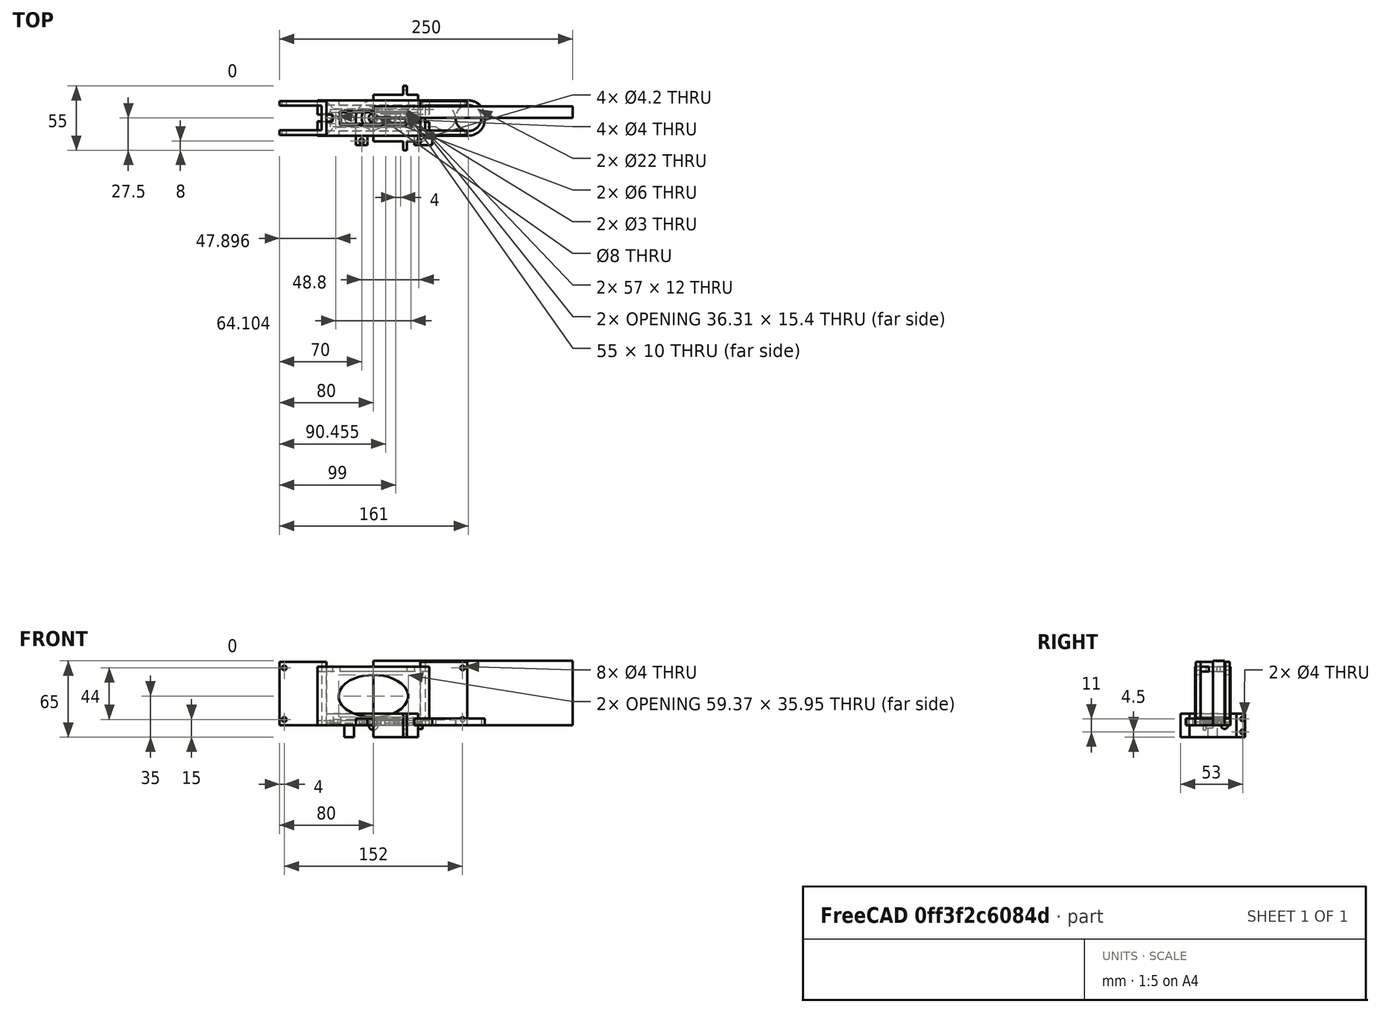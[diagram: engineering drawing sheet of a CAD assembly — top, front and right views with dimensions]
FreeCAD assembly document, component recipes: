
FREECAD ASSEMBLY — COMPONENT RECIPES ("assembly_05")

This assembly document has 12 components, labeled P0..P11 below (a component is one placed body or linked part). 12 of them carry a construction recipe — the FreeCAD feature program that regenerates the part from scratch, quoted from this document or its linked companion documents; the rest are supplied as boundary geometry only. No exploded tour is included for this assembly.
COMPONENT P0 — recipe-attached ("lower_leg", modeled in this document).
Construction recipe (the document's own serialized feature program — sketch geometry with constraints, then the solid features built on it; lengths are millimeters unless a unit is written):

FEATURE [Sketcher::SketchObject] Sketch
  FullyConstrained = true
  MapMode = 5
  Support = -> [XY_Plane001]
  sketch-geometry (4):
    g0: LineSegment StartX=53.3856 StartY=-7.50386 StartZ=0 EndX=-36.6144 EndY=-7.50386 EndZ=0
    g1: LineSegment StartX=-36.6144 StartY=-7.50386 StartZ=0 EndX=-36.6144 EndY=7.49614 EndZ=0
    g2: LineSegment StartX=-36.6144 StartY=7.49614 StartZ=0 EndX=53.3856 EndY=7.50386 EndZ=0
    g3: ArcOfCircle CenterX=59.9956 CenterY=0 CenterZ=0 NormalX=0 NormalY=0 NormalZ=1 AngleXU=0 Radius=10 StartAngle=3.99024 EndAngle=8.57613
  constraints (13):
    c: Coincident(g0,g1)
    c: Coincident(g1,g2)
    c: Horizontal(g0)
    c: Vertical(g1)
    c: Diameter(g3) = 20
    c: PointOnObject(g3,g-1)
    c: Coincident(g2,g3)
    c: Coincident(g0,g3)
    c: DistanceX(g0,g0) = 90
    c: DistanceY(g1,g1) = 15
    c: DistanceX(g2,g3) = 6.61
    c: DistanceX(g2) = 53.3856
    c: DistanceX(g2,g2) = 90
FEATURE [PartDesign::Pad] Pad
  Direction = (0,0,1)
  Length = 5
  Length2 = 10
  Profile = -> Sketch
  ReferenceAxis = -> Sketch [N_Axis]
  Type = 0
FEATURE [Sketcher::SketchObject] Sketch047
  ExternalGeometry = -> [Pad]
  FullyConstrained = true
  MapMode = 5
  Placement = pos=(0,0,0) rot=(1,0,0;3.14159rad)
  Support = -> [Pad]
  sketch-geometry (1):
    g0: Circle CenterX=-20.6144 CenterY=0 CenterZ=0 NormalX=0 NormalY=0 NormalZ=1 AngleXU=0 Radius=4.1
  constraints (3):
    c: PointOnObject(g0,g-1)
    c: DistanceX(g-3,g0) = 16
    c: Diameter(g0) = 8.2
FEATURE [PartDesign::Pad] Pad029
  BaseFeature = -> Pad
  Direction = (0,0,-1)
  Length = 10
  Length2 = 10
  Profile = -> Sketch047
  ReferenceAxis = -> Sketch047 [N_Axis]
  Type = 0
FEATURE [Sketcher::SketchObject] Sketch052
  ExternalGeometry = -> [Sketch,Pad029]
  FullyConstrained = true
  MapMode = 5
  Placement = pos=(0,0,0) rot=(1,0,0;3.14159rad)
  Support = -> [Pad029]
  sketch-geometry (1):
    g0: Circle CenterX=-32.1044 CenterY=0 CenterZ=0 NormalX=0 NormalY=0 NormalZ=1 AngleXU=0 Radius=2
  constraints (3):
    c: PointOnObject(g0,g-1)
    c: Diameter(g0) = 4
    c: Distance(g0,g-3) = 4.51
FEATURE [PartDesign::Pocket] Pocket
  BaseFeature = -> Pad029
  Direction = (0,0,1)
  Length = 5
  Length2 = 5
  Profile = -> Sketch052
  ReferenceAxis = -> Sketch052 [N_Axis]
  Type = 0
FEATURE [PartDesign::CoordinateSystem] Local_CS014
  AttacherType = Attacher::AttachEngine3D
  MapMode = 45
  Placement = pos=(-32.1044,0,2.5) rot=(0,0,1;0rad)
  Support = -> [Pocket]
FEATURE [PartDesign::CoordinateSystem] Local_CS015
  AttacherType = Attacher::AttachEngine3D
  MapMode = 45
  Placement = pos=(-20.6144,1e-16,-10) rot=(0,0,1;0rad)
  Support = -> [Pocket]
FEATURE [PartDesign::CoordinateSystem] Local_CS039
  AttacherType = Attacher::AttachEngine3D
  MapMode = 11
  Placement = pos=(-20.6144,0,0) rot=(0.707107,-0.707107,0;3.14159rad)
  Support = -> [Sketch047]
FEATURE [PartDesign::Body] Body  label="lower_leg"
  Group = -> [Sketch,Pad,Sketch047,Pad029,Sketch052,Pocket,Local_CS014,Local_CS015,Local_CS039]
  Origin = -> Origin001
  Tip = -> Pocket
COMPONENT P1 — recipe-attached ("leg_connector", modeled in this document).
Construction recipe (the document's own serialized feature program — sketch geometry with constraints, then the solid features built on it; lengths are millimeters unless a unit is written):

FEATURE [Sketcher::SketchObject] Sketch049
  FullyConstrained = true
  MapMode = 5
  Support = -> [XY_Plane014]
  sketch-geometry (4):
    g0: LineSegment StartX=-40 StartY=5 StartZ=0 EndX=40 EndY=5 EndZ=0
    g1: LineSegment StartX=40 StartY=5 StartZ=0 EndX=40 EndY=-5 EndZ=0
    g2: LineSegment StartX=40 StartY=-5 StartZ=0 EndX=-40 EndY=-5 EndZ=0
    g3: LineSegment StartX=-40 StartY=-5 StartZ=0 EndX=-40 EndY=5 EndZ=0
  constraints (10):
    c: Coincident(g0,g1)
    c: Coincident(g1,g2)
    c: Coincident(g2,g3)
    c: Coincident(g3,g0)
    c: Horizontal(g2)
    c: Vertical(g3)
    c: Symmetric(g0,g1,g-1)
    c: Symmetric(g0,g0,g-2)
    c: DistanceX(g0,g0) = 80
    c: DistanceY(g1,g1) = 10
FEATURE [PartDesign::Pad] Pad030
  Direction = (0,0,1)
  Length = 2
  Length2 = 10
  Profile = -> Sketch049
  ReferenceAxis = -> Sketch049 [N_Axis]
  Type = 0
FEATURE [Sketcher::SketchObject] Sketch050
  ExternalGeometry = -> [Pad030]
  FullyConstrained = true
  MapMode = 5
  Placement = pos=(0,0,2) rot=(0,0,1;0rad)
  Support = -> [Pad030]
  sketch-geometry (2):
    g0: Circle CenterX=-32 CenterY=0 CenterZ=0 NormalX=0 NormalY=0 NormalZ=1 AngleXU=0 Radius=2
    g1: Circle CenterX=32 CenterY=0 CenterZ=0 NormalX=0 NormalY=0 NormalZ=1 AngleXU=0 Radius=2
  constraints (5):
    c: PointOnObject(g0,g-1)
    c: Diameter(g1) = 4
    c: Diameter(g0) = 4
    c: Symmetric(g1,g0,g-2)
    c: DistanceX(g0,g1) = 64
FEATURE [PartDesign::Pocket] Pocket023
  BaseFeature = -> Pad030
  Direction = (0,0,-1)
  Length = 5
  Length2 = 5
  Profile = -> Sketch050
  ReferenceAxis = -> Sketch050 [N_Axis]
  Type = 0
FEATURE [PartDesign::Fillet] Fillet
  Base = -> Pocket023 [Edge8,Edge2,Edge5,Edge1]
  BaseFeature = -> Pocket023
  Radius = 4
  SupportTransform = false
  UseAllEdges = false
FEATURE [PartDesign::CoordinateSystem] Local_CS
  AttacherType = Attacher::AttachEngine3D
  MapMode = 45
  Placement = pos=(32,0,1) rot=(0,0,1;0rad)
  Support = -> [Fillet]
FEATURE [PartDesign::CoordinateSystem] Local_CS019
  AttacherType = Attacher::AttachEngine3D
  MapMode = 45
  Placement = pos=(-32,0,1) rot=(0,0,1;0rad)
  Support = -> [Fillet]
FEATURE [PartDesign::Body] Body012  label="leg_connector"
  Group = -> [Sketch049,Pad030,Sketch050,Pocket023,Fillet,Local_CS,Local_CS019]
  Origin = -> Origin014
  Tip = -> Fillet
COMPONENT P2 — recipe-attached ("servo", modeled in this document).
Construction recipe (the document's own serialized feature program — sketch geometry with constraints, then the solid features built on it; lengths are millimeters unless a unit is written):

FEATURE [PartDesign::Plane] DatumPlane
  AttachmentOffset = pos=(0,0,25.5) rot=(0,0,1;0rad)
  Length = 65.4881
  MapMode = 5
  Placement = pos=(25.5,-5.7e-15,5.7e-15) rot=(0.57735,0.57735,0.57735;2.0944rad)
  ResizeMode = 0
  Support = -> [YZ_Plane015]
  Width = 60.4881
FEATURE [Sketcher::SketchObject] Sketch055
  FullyConstrained = true
  MapMode = 5
  Placement = pos=(25.5,-5.7e-15,5.7e-15) rot=(0.57735,0.57735,0.57735;2.0944rad)
  Support = -> [DatumPlane]
  sketch-geometry (8):
    g0: LineSegment StartX=-27.5 StartY=10 StartZ=0 EndX=27.5 EndY=10 EndZ=0
    g1: LineSegment StartX=27.5 StartY=10 StartZ=0 EndX=27.5 EndY=-10 EndZ=0
    g2: LineSegment StartX=27.5 StartY=-10 StartZ=0 EndX=-27.5 EndY=-10 EndZ=0
    g3: LineSegment StartX=-27.5 StartY=-10 StartZ=0 EndX=-27.5 EndY=10 EndZ=0
    g4: Circle CenterX=-25.5 CenterY=5.5 CenterZ=0 NormalX=0 NormalY=0 NormalZ=1 AngleXU=0 Radius=2
    g5: Circle CenterX=-25.5 CenterY=-5.5 CenterZ=0 NormalX=0 NormalY=0 NormalZ=1 AngleXU=0 Radius=2
    g6: Circle CenterX=25.5 CenterY=5.5 CenterZ=0 NormalX=0 NormalY=0 NormalZ=1 AngleXU=0 Radius=2
    g7: Circle CenterX=25.5 CenterY=-5.5 CenterZ=0 NormalX=0 NormalY=0 NormalZ=1 AngleXU=0 Radius=2
  constraints (22):
    c: Coincident(g0,g1)
    c: Coincident(g1,g2)
    c: Coincident(g2,g3)
    c: Coincident(g3,g0)
    c: Horizontal(g2)
    c: Vertical(g3)
    c: Symmetric(g0,g0,g-2)
    c: Symmetric(g0,g1,g-1)
    c: DistanceY(g1,g1) = 20
    c: DistanceX(g0,g0) = 55
    c: Diameter(g4) = 4
    c: Diameter(g5) = 4
    c: Diameter(g6) = 4
    c: Diameter(g7) = 4
    c: DistanceY(g4,g0) = 4.5
    c: DistanceY(g6,g0) = 4.5
    c: DistanceY(g2,g5) = 4.5
    c: DistanceY(g1,g7) = 4.5
    c: DistanceX(g0,g4) = 2
    c: DistanceX(g2,g5) = 2
    c: DistanceX(g6,g0) = 2
    c: DistanceX(g7,g1) = 2
FEATURE [Sketcher::SketchObject] Sketch054
  FullyConstrained = true
  MapMode = 5
  Placement = pos=(0,0,0) rot=(0.57735,0.57735,0.57735;2.0944rad)
  Support = -> [YZ_Plane015]
  sketch-geometry (4):
    g0: LineSegment StartX=-20 StartY=10 StartZ=0 EndX=20 EndY=10 EndZ=0
    g1: LineSegment StartX=20 StartY=10 StartZ=0 EndX=20 EndY=-10 EndZ=0
    g2: LineSegment StartX=20 StartY=-10 StartZ=0 EndX=-20 EndY=-10 EndZ=0
    g3: LineSegment StartX=-20 StartY=-10 StartZ=0 EndX=-20 EndY=10 EndZ=0
  constraints (10):
    c: Coincident(g0,g1)
    c: Coincident(g1,g2)
    c: Coincident(g2,g3)
    c: Coincident(g3,g0)
    c: Horizontal(g2)
    c: Vertical(g3)
    c: Symmetric(g0,g0,g-2)
    c: Symmetric(g0,g1,g-1)
    c: DistanceX(g0,g0) = 40
    c: DistanceY(g1,g1) = 20
FEATURE [PartDesign::Pad] Pad034
  Direction = (1,-2e-16,3e-16)
  Length = 38
  Length2 = 10
  Placement = pos=(0,0,0) rot=(0.57735,0.57735,0.57735;2.0944rad)
  Profile = -> Sketch054
  ReferenceAxis = -> Sketch054 [N_Axis]
  Type = 0
FEATURE [PartDesign::Pad] Pad035
  BaseFeature = -> Pad034
  Direction = (1,-1e-16,1e-16)
  Length = 3
  Length2 = 10
  Placement = pos=(0,0,0) rot=(0.57735,0.57735,0.57735;2.0944rad)
  Profile = -> Sketch055
  ReferenceAxis = -> Sketch055 [N_Axis]
  Type = 0
FEATURE [Sketcher::SketchObject] Sketch056
  ExternalGeometry = -> [Pad035]
  FullyConstrained = true
  MapMode = 5
  Placement = pos=(38,-8.4e-15,8.4e-15) rot=(0.57735,0.57735,0.57735;2.0944rad)
  Support = -> [Pad035]
  sketch-geometry (1):
    g0: Circle CenterX=10 CenterY=0 CenterZ=0 NormalX=0 NormalY=0 NormalZ=1 AngleXU=0 Radius=3
  constraints (3):
    c: PointOnObject(g0,g-1)
    c: Diameter(g0) = 6
    c: DistanceX(g0,g-3) = 10
FEATURE [PartDesign::Pad] Pad036
  BaseFeature = -> Pad035
  Direction = (1,-9e-16,6e-16)
  Length = 4
  Length2 = 10
  Placement = pos=(0,0,0) rot=(0.57735,0.57735,0.57735;2.0944rad)
  Profile = -> Sketch056
  ReferenceAxis = -> Sketch056 [N_Axis]
  Type = 0
FEATURE [PartDesign::CoordinateSystem] Local_CS009
  AttacherType = Attacher::AttachEngine3D
  MapMode = 45
  Placement = pos=(27,25.5,-5.5) rot=(0.57735,0.57735,0.57735;2.0944rad)
  Support = -> [Pad036]
FEATURE [PartDesign::CoordinateSystem] Local_CS010
  AttacherType = Attacher::AttachEngine3D
  MapMode = 45
  Placement = pos=(27,25.5,5.5) rot=(0.57735,0.57735,0.57735;2.0944rad)
  Support = -> [Pad036]
FEATURE [PartDesign::CoordinateSystem] Local_CS011  label="lcs_lever_adapter"
  AttacherType = Attacher::AttachEngine3D
  MapMode = 45
  Placement = pos=(42,10,1.82e-14) rot=(0.57735,0.57735,0.57735;2.0944rad)
  Support = -> [Pad036]
FEATURE [PartDesign::CoordinateSystem] Local_CS020
  AttacherType = Attacher::AttachEngine3D
  MapMode = 45
  Placement = pos=(0,-1e-16,7e-16) rot=(0.707107,0,0.707107;3.14159rad)
  Support = -> [Pad036]
FEATURE [PartDesign::CoordinateSystem] Local_CS043  label="servo_bottom_lcs"
  AttacherType = Attacher::AttachEngine3D
  MapMode = 5
  Placement = pos=(0,0,0) rot=(0.57735,0.57735,-0.57735;4.18879rad)
  Support = -> [Pad036]
FEATURE [PartDesign::Body] Body013  label="servo"
  Group = -> [Sketch054,Pad034,DatumPlane,Sketch055,Pad035,Sketch056,Pad036,Local_CS009,Local_CS010,Local_CS011,Local_CS020,Local_CS043]
  Origin = -> Origin015
  Tip = -> Pad036
COMPONENT P3 — recipe-attached ("connector_bolt", modeled in this document).
Construction recipe (the document's own serialized feature program — sketch geometry with constraints, then the solid features built on it; lengths are millimeters unless a unit is written):

FEATURE [Sketcher::SketchObject] Sketch077
  FullyConstrained = true
  MapMode = 5
  Placement = pos=(0,0,0) rot=(1,0,0;1.5708rad)
  Support = -> [XZ_Plane018]
  sketch-geometry (1):
    g0: Circle CenterX=0 CenterY=0 CenterZ=0 NormalX=0 NormalY=0 NormalZ=1 AngleXU=0 Radius=2
  constraints (2):
    c: Coincident(g0,g-1)
    c: Diameter(g0) = 4
FEATURE [PartDesign::Pad] Pad048
  Direction = (0,-1,2e-16)
  Length = 6
  Length2 = 10
  Placement = pos=(0,0,0) rot=(1,0,0;1.5708rad)
  Profile = -> Sketch077
  ReferenceAxis = -> Sketch077 [N_Axis]
  Type = 0
FEATURE [Sketcher::SketchObject] Sketch078
  FullyConstrained = true
  MapMode = 5
  Placement = pos=(0,-6,1.3e-15) rot=(1,0,0;1.5708rad)
  Support = -> [Pad048]
  sketch-geometry (1):
    g0: Circle CenterX=0 CenterY=0 CenterZ=0 NormalX=0 NormalY=0 NormalZ=1 AngleXU=0 Radius=4
  constraints (2):
    c: Coincident(g0,g-1)
    c: Diameter(g0) = 8
FEATURE [PartDesign::Pad] Pad049
  BaseFeature = -> Pad048
  Direction = (0,-1,2e-16)
  Length = 2
  Length2 = 10
  Placement = pos=(0,0,0) rot=(1,0,0;1.5708rad)
  Profile = -> Sketch078
  ReferenceAxis = -> Sketch078 [N_Axis]
  Type = 0
FEATURE [PartDesign::CoordinateSystem] Local_CS025
  AttacherType = Attacher::AttachEngine3D
  MapMode = 45
  Placement = pos=(0,-3,1.2e-15) rot=(0,0.707107,0.707107;3.14159rad)
  Support = -> [Pad049]
FEATURE [PartDesign::Body] Body016  label="connector_bolt"
  Group = -> [Sketch077,Pad048,Sketch078,Pad049,Local_CS025]
  Origin = -> Origin018
  Tip = -> Pad049
COMPONENT P4 — recipe-attached ("upper_leg_left", modeled in this document).
Construction recipe (the document's own serialized feature program — sketch geometry with constraints, then the solid features built on it; lengths are millimeters unless a unit is written):

FEATURE [Sketcher::SketchObject] Sketch084
  FullyConstrained = false
  MapMode = 5
  Placement = pos=(0,0,0) rot=(1,0,0;3.14159rad)
  sketch-geometry (4):
    g0: LineSegment StartX=13.6097 StartY=7.7 StartZ=0 EndX=28.6097 EndY=7.7 EndZ=0
    g1: LineSegment StartX=28.6097 StartY=7.7 StartZ=0 EndX=28.6097 EndY=-7.7 EndZ=0
    g2: LineSegment StartX=28.6097 StartY=-7.7 StartZ=0 EndX=13.6097 EndY=-7.7 EndZ=0
    g3: LineSegment StartX=13.6097 StartY=-7.7 StartZ=0 EndX=13.6097 EndY=7.7 EndZ=0
  constraints (8):
    c: Coincident(g0,g1)
    c: Coincident(g1,g2)
    c: Coincident(g2,g3)
    c: Coincident(g3,g0)
    c: Horizontal(g0)
    c: Horizontal(g2)
    c: Vertical(g1)
    c: Vertical(g3)
FEATURE [Sketcher::SketchObject] Sketch079
  FullyConstrained = false
  MapMode = 5
  Support = -> [XY_Plane019]
  sketch-geometry (12):
    g0: ArcOfCircle CenterX=0 CenterY=0 CenterZ=0 NormalX=0 NormalY=0 NormalZ=1 AngleXU=0 Radius=7.7 StartAngle=1.5708 EndAngle=4.71239
    g1: LineSegment StartX=28.6097 StartY=-3.8 StartZ=0 EndX=13.6097 EndY=-3.8 EndZ=0
    g2: LineSegment StartX=13.6097 StartY=3.8 StartZ=0 EndX=28.6097 EndY=3.8 EndZ=0
    g3: LineSegment StartX=28.6097 StartY=3.8 StartZ=0 EndX=28.6097 EndY=-3.8 EndZ=0
    g4: LineSegment StartX=-1.2e-15 StartY=7.7 StartZ=0 EndX=13.6097 EndY=7.7 EndZ=0
    g5: LineSegment StartX=13.6097 StartY=7.7 StartZ=0 EndX=13.6097 EndY=3.8 EndZ=0
    g6: LineSegment StartX=-1.4e-15 StartY=-7.7 StartZ=0 EndX=13.6097 EndY=-7.7 EndZ=0
    g7: LineSegment StartX=13.6097 StartY=-7.7 StartZ=0 EndX=13.6097 EndY=-3.8 EndZ=0
    g8: LineSegment StartX=-15 StartY=15 StartZ=0 EndX=95 EndY=15 EndZ=0
    g9: LineSegment StartX=95 StartY=15 StartZ=0 EndX=95 EndY=-15 EndZ=0
    g10: LineSegment StartX=95 StartY=-15 StartZ=0 EndX=-15 EndY=-15 EndZ=0
    g11: LineSegment StartX=-15 StartY=-15 StartZ=0 EndX=-15 EndY=15 EndZ=0
  constraints (31):
    c: Coincident(g0,g-1)
    c: Diameter(g0) = 15.4
    c: Coincident(g2,g3)
    c: Coincident(g3,g1)
    c: Horizontal(g1)
    c: Horizontal(g2)
    c: Symmetric(g1,g2,g-1)
    c: DistanceY(g3,g3) = 7.6
    c: Horizontal(g4)
    c: Coincident(g4,g5)
    c: Vertical(g5)
    c: DistanceX(g5,g2) = 15
    c: Horizontal(g6)
    c: Coincident(g6,g7)
    c: Vertical(g7)
    c: DistanceX(g7,g1) = 15
    c: Tangent(g0,g4) = 1.5708
    c: Coincident(g2,g5)
    c: Coincident(g1,g7)
    c: Tangent(g0,g6) = -1.5708
    c: Coincident(g8,g9)
    c: Coincident(g9,g10)
    c: Coincident(g10,g11)
    c: Coincident(g11,g8)
    c: Horizontal(g8)
    c: Horizontal(g10)
    c: Vertical(g9)
    c: Symmetric(g8,g10,g-1)
    c: DistanceY(g11,g11) = 30
    c: DistanceX(g10,g-1) = 15
    c: DistanceX(g-1,g9) = 95
FEATURE [PartDesign::Pad] Pad050
  Direction = (0,0,1)
  Length = 6
  Length2 = 10
  Profile = -> Sketch079
  ReferenceAxis = -> Sketch079 [N_Axis]
  Type = 0
FEATURE [Sketcher::SketchObject] Sketch080
  ExternalGeometry = -> [Pad050]
  FullyConstrained = true
  MapMode = 5
  Placement = pos=(0,-15,0) rot=(1,0,0;1.5708rad)
  Support = -> [Pad050]
  sketch-geometry (4):
    g0: LineSegment StartX=-15 StartY=6 StartZ=0 EndX=50 EndY=6 EndZ=0
    g1: LineSegment StartX=50 StartY=6 StartZ=0 EndX=50 EndY=0 EndZ=0
    g2: LineSegment StartX=50 StartY=0 StartZ=0 EndX=-15 EndY=0 EndZ=0
    g3: LineSegment StartX=-15 StartY=0 StartZ=0 EndX=-15 EndY=6 EndZ=0
  constraints (11):
    c: Coincident(g0,g1)
    c: Coincident(g1,g2)
    c: Coincident(g2,g3)
    c: Coincident(g3,g0)
    c: Horizontal(g0)
    c: Horizontal(g2)
    c: Vertical(g1)
    c: Vertical(g3)
    c: Coincident(g0,g-4)
    c: PointOnObject(g1,g-5)
    c: DistanceX(g0,g0) = 65
FEATURE [Sketcher::SketchObject] Sketch081
  FullyConstrained = false
  MapMode = 5
  Placement = pos=(0,0,-3e-15) rot=(1,0,0;3.14159rad)
  sketch-geometry (2):
    g0: Circle CenterX=-10 CenterY=19.5 CenterZ=0 NormalX=0 NormalY=0 NormalZ=1 AngleXU=0 Radius=2.1
    g1: Circle CenterX=38.8 CenterY=19.5 CenterZ=0 NormalX=0 NormalY=0 NormalZ=1 AngleXU=0 Radius=2.1
  constraints (5):
    c: DistanceY(g0,g1) = 0
    c: DistanceX(g0,g1) = 48.8
    c: Diameter(g1) = 4.2
    c: Diameter(g0) = 4.2
    c: DistanceY(g-1,g0) = 19.5
FEATURE [PartDesign::Pad] Pad051
  BaseFeature = -> Pad050
  Direction = (0,-1,2e-16)
  Length = 8
  Length2 = 10
  Profile = -> Sketch080
  ReferenceAxis = -> Sketch080 [N_Axis]
  Type = 0
FEATURE [PartDesign::Pocket] Pocket024
  BaseFeature = -> Pad051
  Direction = (0,0,1)
  Length = 5
  Length2 = 5
  Midplane = true
  Profile = -> Sketch081
  ReferenceAxis = -> Sketch081 [N_Axis]
  Type = 1
FEATURE [Sketcher::SketchObject] Sketch082
  ExternalGeometry = -> [Sketch080,Pocket024]
  FullyConstrained = false
  MapMode = 5
  Placement = pos=(0,1.3e-15,6) rot=(0,0,1;0rad)
  Support = -> [Pocket024]
  sketch-geometry (4):
    g0: LineSegment StartX=-5 StartY=-34 StartZ=0 EndX=35 EndY=-34 EndZ=0
    g1: LineSegment StartX=35 StartY=-34 StartZ=0 EndX=35 EndY=-15 EndZ=0
    g2: LineSegment StartX=35 StartY=-15 StartZ=0 EndX=-5 EndY=-15 EndZ=0
    g3: LineSegment StartX=-5 StartY=-15 StartZ=0 EndX=-5 EndY=-34 EndZ=0
  constraints (11):
    c: Coincident(g0,g1)
    c: Coincident(g1,g2)
    c: Coincident(g2,g3)
    c: Coincident(g3,g0)
    c: Horizontal(g0)
    c: Horizontal(g2)
    c: Vertical(g1)
    c: Vertical(g3)
    c: DistanceX(g-5,g2) = 10
    c: PointOnObject(g2,g-3)
    c: DistanceX(g0,g0) = 40
FEATURE [PartDesign::Pocket] Pocket025
  BaseFeature = -> Pocket024
  Direction = (0,-2e-16,-1)
  Length = 3
  Length2 = 5
  Midplane = true
  Profile = -> Sketch082
  ReferenceAxis = -> Sketch082 [N_Axis]
  Type = 1
FEATURE [Sketcher::SketchObject] Sketch083
  ExternalGeometry = -> [Pocket025]
  FullyConstrained = true
  MapMode = 5
  Placement = pos=(0,0,6) rot=(0,0,1;0rad)
  Support = -> [Pocket025]
  sketch-geometry (1):
    g0: Circle CenterX=81 CenterY=0 CenterZ=0 NormalX=0 NormalY=0 NormalZ=1 AngleXU=0 Radius=11
  constraints (3):
    c: PointOnObject(g0,g-1)
    c: Diameter(g0) = 22
    c: DistanceX(g0,g-3) = 14
FEATURE [PartDesign::Pocket] Pocket026
  BaseFeature = -> Pocket025
  Direction = (0,0,-1)
  Length = 5
  Length2 = 5
  Midplane = true
  Profile = -> Sketch083
  ReferenceAxis = -> Sketch083 [N_Axis]
  Type = 1
FEATURE [PartDesign::Fillet] Fillet014
  Base = -> Pocket026 [Edge8,Edge2]
  BaseFeature = -> Pocket026
  Radius = 14
  SupportTransform = false
  UseAllEdges = false
FEATURE [PartDesign::Fillet] Fillet015
  Base = -> Fillet014 [Edge3]
  BaseFeature = -> Fillet014
  Radius = 15
  SupportTransform = false
  UseAllEdges = false
FEATURE [PartDesign::Fillet] Fillet016
  Base = -> Fillet015
  BaseFeature = -> Fillet015
  Radius = 3
  SupportTransform = false
  UseAllEdges = false
FEATURE [PartDesign::Pad] Pad052
  BaseFeature = -> Fillet016
  Direction = (0,0,-1)
  Length = 2
  Length2 = 10
  Profile = -> Sketch084
  ReferenceAxis = -> Sketch084 [N_Axis]
  Reversed = true
  Type = 0
FEATURE [PartDesign::CoordinateSystem] Local_CS026
  AttacherType = Attacher::AttachEngine3D
  MapMode = 45
  Placement = pos=(38.8,-19.5,3) rot=(0,0,1;0rad)
  Support = -> [Pad052]
FEATURE [PartDesign::CoordinateSystem] Local_CS027
  AttacherType = Attacher::AttachEngine3D
  MapMode = 45
  Placement = pos=(-10,-19.5,3) rot=(0,0,1;0rad)
  Support = -> [Pad052]
FEATURE [PartDesign::CoordinateSystem] Local_CS028
  AttacherType = Attacher::AttachEngine3D
  MapMode = 45
  Placement = pos=(81,-8e-16,3) rot=(0,0,1;0rad)
  Support = -> [Pad052]
FEATURE [PartDesign::CoordinateSystem] Local_CS029
  AttacherType = Attacher::AttachEngine3D
  MapMode = 45
  Placement = pos=(1.29631,4e-16,3) rot=(0,0,1;0rad)
  Support = -> [Pad052]
FEATURE [PartDesign::Body] Body017  label="upper_leg_left"
  Group = -> [Sketch079,Pad050,Sketch080,Pad051,Sketch081,Pocket024,Sketch082,Pocket025,Sketch083,Pocket026,Fillet014,Fillet015,Fillet016,Sketch084,Pad052,Local_CS026,Local_CS027,Local_CS028,Local_CS029]
  Origin = -> Origin019
  Tip = -> Pad052
COMPONENT P5 — recipe-attached ("upper_leg_right", modeled in this document).
Construction recipe (the document's own serialized feature program — sketch geometry with constraints, then the solid features built on it; lengths are millimeters unless a unit is written):

FEATURE [Sketcher::SketchObject] Sketch085
  FullyConstrained = false
  MapMode = 5
  Support = -> [XY_Plane020]
  sketch-geometry (12):
    g0: ArcOfCircle CenterX=0 CenterY=0 CenterZ=0 NormalX=0 NormalY=0 NormalZ=1 AngleXU=0 Radius=7.7 StartAngle=1.5708 EndAngle=4.71239
    g1: LineSegment StartX=28.6097 StartY=-3.8 StartZ=0 EndX=13.6097 EndY=-3.8 EndZ=0
    g2: LineSegment StartX=13.6097 StartY=3.8 StartZ=0 EndX=28.6097 EndY=3.8 EndZ=0
    g3: LineSegment StartX=28.6097 StartY=3.8 StartZ=0 EndX=28.6097 EndY=-3.8 EndZ=0
    g4: LineSegment StartX=-1.2e-15 StartY=7.7 StartZ=0 EndX=13.6097 EndY=7.7 EndZ=0
    g5: LineSegment StartX=13.6097 StartY=7.7 StartZ=0 EndX=13.6097 EndY=3.8 EndZ=0
    g6: LineSegment StartX=-1.4e-15 StartY=-7.7 StartZ=0 EndX=13.6097 EndY=-7.7 EndZ=0
    g7: LineSegment StartX=13.6097 StartY=-7.7 StartZ=0 EndX=13.6097 EndY=-3.8 EndZ=0
    g8: LineSegment StartX=-15 StartY=15 StartZ=0 EndX=95 EndY=15 EndZ=0
    g9: LineSegment StartX=95 StartY=15 StartZ=0 EndX=95 EndY=-15 EndZ=0
    g10: LineSegment StartX=95 StartY=-15 StartZ=0 EndX=-15 EndY=-15 EndZ=0
    g11: LineSegment StartX=-15 StartY=-15 StartZ=0 EndX=-15 EndY=15 EndZ=0
  constraints (31):
    c: Coincident(g0,g-1)
    c: Diameter(g0) = 15.4
    c: Coincident(g2,g3)
    c: Coincident(g3,g1)
    c: Horizontal(g1)
    c: Horizontal(g2)
    c: Symmetric(g1,g2,g-1)
    c: DistanceY(g3,g3) = 7.6
    c: Horizontal(g4)
    c: Coincident(g4,g5)
    c: Vertical(g5)
    c: DistanceX(g5,g2) = 15
    c: Horizontal(g6)
    c: Coincident(g6,g7)
    c: Vertical(g7)
    c: DistanceX(g7,g1) = 15
    c: Tangent(g0,g4) = 1.5708
    c: Coincident(g2,g5)
    c: Coincident(g1,g7)
    c: Tangent(g0,g6) = -1.5708
    c: Coincident(g8,g9)
    c: Coincident(g9,g10)
    c: Coincident(g10,g11)
    c: Coincident(g11,g8)
    c: Horizontal(g8)
    c: Horizontal(g10)
    c: Vertical(g9)
    c: Symmetric(g8,g10,g-1)
    c: DistanceY(g11,g11) = 30
    c: DistanceX(g10,g-1) = 15
    c: DistanceX(g-1,g9) = 95
FEATURE [PartDesign::Pad] Pad053
  Direction = (0,0,1)
  Length = 6
  Length2 = 10
  Profile = -> Sketch085
  ReferenceAxis = -> Sketch085 [N_Axis]
  Type = 0
FEATURE [Sketcher::SketchObject] Sketch086
  ExternalGeometry = -> [Pad053]
  FullyConstrained = true
  MapMode = 5
  Placement = pos=(0,-15,0) rot=(1,0,0;1.5708rad)
  Support = -> [Pad053]
  sketch-geometry (4):
    g0: LineSegment StartX=-15 StartY=6 StartZ=0 EndX=50 EndY=6 EndZ=0
    g1: LineSegment StartX=50 StartY=6 StartZ=0 EndX=50 EndY=0 EndZ=0
    g2: LineSegment StartX=50 StartY=0 StartZ=0 EndX=-15 EndY=0 EndZ=0
    g3: LineSegment StartX=-15 StartY=0 StartZ=0 EndX=-15 EndY=6 EndZ=0
  constraints (11):
    c: Coincident(g0,g1)
    c: Coincident(g1,g2)
    c: Coincident(g2,g3)
    c: Coincident(g3,g0)
    c: Horizontal(g0)
    c: Horizontal(g2)
    c: Vertical(g1)
    c: Vertical(g3)
    c: Coincident(g0,g-4)
    c: PointOnObject(g1,g-5)
    c: DistanceX(g0,g0) = 65
FEATURE [Sketcher::SketchObject] Sketch087
  FullyConstrained = false
  MapMode = 5
  Placement = pos=(0,0,-3e-15) rot=(1,0,0;3.14159rad)
  sketch-geometry (2):
    g0: Circle CenterX=-10 CenterY=19.5 CenterZ=0 NormalX=0 NormalY=0 NormalZ=1 AngleXU=0 Radius=2.1
    g1: Circle CenterX=38.8 CenterY=19.5 CenterZ=0 NormalX=0 NormalY=0 NormalZ=1 AngleXU=0 Radius=2.1
  constraints (5):
    c: DistanceY(g0,g1) = 0
    c: DistanceX(g0,g1) = 48.8
    c: Diameter(g1) = 4.2
    c: Diameter(g0) = 4.2
    c: DistanceY(g-1,g0) = 19.5
FEATURE [PartDesign::Pad] Pad054
  BaseFeature = -> Pad053
  Direction = (0,-1,2e-16)
  Length = 8
  Length2 = 10
  Profile = -> Sketch086
  ReferenceAxis = -> Sketch086 [N_Axis]
  Type = 0
FEATURE [PartDesign::Pocket] Pocket027
  BaseFeature = -> Pad054
  Direction = (0,0,1)
  Length = 5
  Length2 = 5
  Midplane = true
  Profile = -> Sketch087
  ReferenceAxis = -> Sketch087 [N_Axis]
  Type = 1
FEATURE [Sketcher::SketchObject] Sketch088
  ExternalGeometry = -> [Sketch086,Pocket027]
  FullyConstrained = false
  MapMode = 5
  Placement = pos=(0,1.3e-15,6) rot=(0,0,1;0rad)
  Support = -> [Pocket027]
  sketch-geometry (4):
    g0: LineSegment StartX=-5 StartY=-34 StartZ=0 EndX=35 EndY=-34 EndZ=0
    g1: LineSegment StartX=35 StartY=-34 StartZ=0 EndX=35 EndY=-15 EndZ=0
    g2: LineSegment StartX=35 StartY=-15 StartZ=0 EndX=-5 EndY=-15 EndZ=0
    g3: LineSegment StartX=-5 StartY=-15 StartZ=0 EndX=-5 EndY=-34 EndZ=0
  constraints (11):
    c: Coincident(g0,g1)
    c: Coincident(g1,g2)
    c: Coincident(g2,g3)
    c: Coincident(g3,g0)
    c: Horizontal(g0)
    c: Horizontal(g2)
    c: Vertical(g1)
    c: Vertical(g3)
    c: DistanceX(g-5,g2) = 10
    c: PointOnObject(g2,g-3)
    c: DistanceX(g0,g0) = 40
FEATURE [PartDesign::Pocket] Pocket028
  BaseFeature = -> Pocket027
  Direction = (0,-2e-16,-1)
  Length = 3
  Length2 = 5
  Midplane = true
  Profile = -> Sketch088
  ReferenceAxis = -> Sketch088 [N_Axis]
  Type = 1
FEATURE [Sketcher::SketchObject] Sketch089
  ExternalGeometry = -> [Pocket028]
  FullyConstrained = true
  MapMode = 5
  Placement = pos=(0,0,6) rot=(0,0,1;0rad)
  Support = -> [Pocket028]
  sketch-geometry (1):
    g0: Circle CenterX=81 CenterY=0 CenterZ=0 NormalX=0 NormalY=0 NormalZ=1 AngleXU=0 Radius=11
  constraints (3):
    c: PointOnObject(g0,g-1)
    c: Diameter(g0) = 22
    c: DistanceX(g0,g-3) = 14
FEATURE [PartDesign::Pocket] Pocket029
  BaseFeature = -> Pocket028
  Direction = (0,0,-1)
  Length = 5
  Length2 = 5
  Midplane = true
  Profile = -> Sketch089
  ReferenceAxis = -> Sketch089 [N_Axis]
  Type = 1
FEATURE [PartDesign::Fillet] Fillet017
  Base = -> Pocket029 [Edge8,Edge2]
  BaseFeature = -> Pocket029
  Radius = 14
  SupportTransform = false
  UseAllEdges = false
FEATURE [PartDesign::Fillet] Fillet018
  Base = -> Fillet017 [Edge3]
  BaseFeature = -> Fillet017
  Radius = 15
  SupportTransform = false
  UseAllEdges = false
FEATURE [PartDesign::Fillet] Fillet019
  Base = -> Fillet018
  BaseFeature = -> Fillet018
  Radius = 3
  SupportTransform = false
  UseAllEdges = false
FEATURE [Sketcher::SketchObject] Sketch091
  ExternalGeometry = -> [Fillet019]
  FullyConstrained = true
  MapMode = 5
  Placement = pos=(0,0,6) rot=(0,0,1;0rad)
  sketch-geometry (4):
    g0: LineSegment StartX=13.6097 StartY=3.8 StartZ=0 EndX=28.6097 EndY=3.8 EndZ=0
    g1: LineSegment StartX=28.6097 StartY=3.8 StartZ=0 EndX=28.6097 EndY=-3.8 EndZ=0
    g2: LineSegment StartX=28.6097 StartY=-3.8 StartZ=0 EndX=13.6097 EndY=-3.8 EndZ=0
    g3: LineSegment StartX=13.6097 StartY=-3.8 StartZ=0 EndX=13.6097 EndY=3.8 EndZ=0
  constraints (10):
    c: Coincident(g0,g1)
    c: Coincident(g1,g2)
    c: Coincident(g2,g3)
    c: Coincident(g3,g0)
    c: Horizontal(g0)
    c: Horizontal(g2)
    c: Vertical(g1)
    c: Vertical(g3)
    c: Coincident(g0,g-3)
    c: Coincident(g1,g-4)
FEATURE [PartDesign::Pad] Pad055
  BaseFeature = -> Fillet019
  Direction = (0,0,1)
  Length = 2
  Length2 = 10
  Profile = -> Sketch091
  ReferenceAxis = -> Sketch091 [N_Axis]
  Reversed = true
  Type = 0
FEATURE [PartDesign::CoordinateSystem] Local_CS030
  AttacherType = Attacher::AttachEngine3D
  MapMode = 45
  Placement = pos=(38.8,-19.5,3) rot=(0,0,1;0rad)
  Support = -> [Pad055]
FEATURE [PartDesign::CoordinateSystem] Local_CS031
  AttacherType = Attacher::AttachEngine3D
  MapMode = 45
  Placement = pos=(-10,-19.5,3) rot=(0,0,1;0rad)
  Support = -> [Pad055]
FEATURE [PartDesign::CoordinateSystem] Local_CS032
  AttacherType = Attacher::AttachEngine3D
  MapMode = 45
  Placement = pos=(1.29631,4e-16,3) rot=(0,0,1;0rad)
  Support = -> [Pad055]
FEATURE [PartDesign::CoordinateSystem] Local_CS033
  AttacherType = Attacher::AttachEngine3D
  MapMode = 45
  Placement = pos=(81,-8e-16,3) rot=(0,0,1;0rad)
  Support = -> [Pad055]
FEATURE [PartDesign::Body] Body018  label="upper_leg_right"
  Group = -> [Sketch085,Pad053,Sketch086,Pad054,Sketch087,Pocket027,Sketch088,Pocket028,Sketch089,Pocket029,Fillet017,Fillet018,Fillet019,Sketch091,Pad055,Local_CS030,Local_CS031,Local_CS032,Local_CS033]
  Origin = -> Origin020
  Tip = -> Pad055
COMPONENT P6 — recipe-attached ("ballbearing", modeled in this document).
Construction recipe (the document's own serialized feature program — sketch geometry with constraints, then the solid features built on it; lengths are millimeters unless a unit is written):

FEATURE [Sketcher::SketchObject] Sketch092
  FullyConstrained = true
  MapMode = 5
  Support = -> [XY_Plane021]
  sketch-geometry (2):
    g0: Circle CenterX=0 CenterY=0 CenterZ=0 NormalX=0 NormalY=0 NormalZ=1 AngleXU=0 Radius=4
    g1: Circle CenterX=0 CenterY=0 CenterZ=0 NormalX=0 NormalY=0 NormalZ=1 AngleXU=0 Radius=10
  constraints (4):
    c: Coincident(g0,g-1)
    c: Coincident(g1,g0)
    c: Diameter(g0) = 8
    c: Diameter(g1) = 20
FEATURE [PartDesign::Pad] Pad056
  Direction = (0,0,1)
  Length = 7
  Length2 = 10
  Profile = -> Sketch092
  ReferenceAxis = -> Sketch092 [N_Axis]
  Type = 0
FEATURE [PartDesign::CoordinateSystem] Local_CS034
  AttacherType = Attacher::AttachEngine3D
  MapMode = 45
  Placement = pos=(0,-1e-16,3.5) rot=(0,0,1;0rad)
  Support = -> [Pad056]
FEATURE [PartDesign::CoordinateSystem] Local_CS038
  AttacherType = Attacher::AttachEngine3D
  MapMode = 11
  Placement = pos=(0,0,0) rot=(0,0,1;1.5708rad)
  Support = -> [Pad056]
FEATURE [PartDesign::Body] Body019  label="ballbearing"
  Group = -> [Sketch092,Pad056,Local_CS034,Local_CS038]
  Origin = -> Origin021
  Tip = -> Pad056
COMPONENT P7 — recipe-attached ("servo_lever", modeled in this document).
Construction recipe (the document's own serialized feature program — sketch geometry with constraints, then the solid features built on it; lengths are millimeters unless a unit is written):

FEATURE [Sketcher::SketchObject] Sketch093
  FullyConstrained = true
  MapMode = 5
  Support = -> [XY_Plane022]
  sketch-geometry (7):
    g0: ArcOfCircle CenterX=0 CenterY=0 CenterZ=0 NormalX=0 NormalY=0 NormalZ=1 AngleXU=0 Radius=7.5 StartAngle=0.523599 EndAngle=5.75959
    g1: LineSegment StartX=6.49519 StartY=3.75 StartZ=0 EndX=23.7452 EndY=3.75 EndZ=0
    g2: LineSegment StartX=23.7452 StartY=-3.75 StartZ=0 EndX=6.49519 EndY=-3.75 EndZ=0
    g3: Circle CenterX=0 CenterY=0 CenterZ=0 NormalX=0 NormalY=0 NormalZ=1 AngleXU=0 Radius=3
    g4: ArcOfCircle CenterX=23.7452 CenterY=0 CenterZ=0 NormalX=0 NormalY=0 NormalZ=1 AngleXU=0 Radius=3.75 StartAngle=4.71239 EndAngle=7.85398
    g5: Circle CenterX=23 CenterY=0 CenterZ=0 NormalX=0 NormalY=0 NormalZ=1 AngleXU=0 Radius=1.5
    g6: Circle CenterX=19 CenterY=0 CenterZ=0 NormalX=0 NormalY=0 NormalZ=1 AngleXU=0 Radius=1.5
  constraints (20):
    c: Coincident(g0,g-1)
    c: Diameter(g0) = 15
    c: Horizontal(g1)
    c: Horizontal(g2)
    c: Coincident(g0,g2)
    c: Coincident(g0,g1)
    c: Coincident(g3,g0)
    c: Diameter(g3) = 6
    c: PointOnObject(g4,g-1)
    c: Tangent(g4,g1) = 1.5708
    c: Coincident(g4,g2)
    c: DistanceX(g1,g1) = 17.25
    c: Diameter(g4) = 7.5
    c: DistanceX(g2,g2) = 17.25
    c: PointOnObject(g5,g-1)
    c: PointOnObject(g6,g-1)
    c: Diameter(g5) = 3
    c: Diameter(g6) = 3
    c: DistanceX(g6,g5) = 4
    c: DistanceX(g0,g6) = 19
FEATURE [PartDesign::Pad] Pad057
  Direction = (0,0,1)
  Length = 4.5
  Length2 = 10
  Profile = -> Sketch093
  ReferenceAxis = -> Sketch093 [N_Axis]
  Type = 0
FEATURE [PartDesign::CoordinateSystem] Local_CS035
  AttacherType = Attacher::AttachEngine3D
  MapMode = 45
  Placement = pos=(-1.3e-15,0,2.25) rot=(0,0,1;0rad)
  Support = -> [Pad057]
FEATURE [PartDesign::CoordinateSystem] Local_CS036
  AttacherType = Attacher::AttachEngine3D
  MapMode = 45
  Placement = pos=(19,0,2.25) rot=(0,0,1;0rad)
  Support = -> [Pad057]
FEATURE [PartDesign::CoordinateSystem] Local_CS037
  AttacherType = Attacher::AttachEngine3D
  MapMode = 45
  Placement = pos=(23,0,2.25) rot=(0,0,1;0rad)
  Support = -> [Pad057]
FEATURE [PartDesign::Body] Body020  label="servo_lever"
  Group = -> [Sketch093,Pad057,Local_CS035,Local_CS036,Local_CS037]
  Origin = -> Origin022
  Tip = -> Pad057
COMPONENT P8 — recipe-attached ("breadboard", modeled in this document).
Construction recipe (the document's own serialized feature program — sketch geometry with constraints, then the solid features built on it; lengths are millimeters unless a unit is written):

FEATURE [PartDesign::AdditiveBox] Box
  AttacherType = Attacher::AttachEngine3D
  Height = 55
  Length = 170
  Width = 10
  expr: Height = Spreadsheet.breadboard_height
  expr: Length = Spreadsheet.breadboard_length
  expr: Width = Spreadsheet.breadboard_width
FEATURE [PartDesign::CoordinateSystem] Local_CS048
  AttacherType = Attacher::AttachEngine3D
  MapMode = 45
  Placement = pos=(170,5,27.5) rot=(0.57735,0.57735,0.57735;2.0944rad)
  Support = -> [Box]
FEATURE [PartDesign::CoordinateSystem] Local_CS049
  AttacherType = Attacher::AttachEngine3D
  MapMode = 45
  Placement = pos=(0,5,27.5) rot=(0.57735,0.57735,0.57735;2.0944rad)
  Support = -> [Box]
FEATURE [PartDesign::Body] Body021  label="breadboard"
  Group = -> [Box,Local_CS048,Local_CS049]
  Origin = -> Origin023
  Tip = -> Box
COMPONENT P9 — recipe-attached ("leg_holder", modeled in this document).
Construction recipe (the document's own serialized feature program — sketch geometry with constraints, then the solid features built on it; lengths are millimeters unless a unit is written):

FEATURE [Sketcher::SketchObject] Sketch096
  FullyConstrained = true
  MapMode = 5
  Support = -> [XY_Plane024]
  expr: Constraints[6] = Spreadsheet.breadboard_height + 40
  expr: Constraints[9] = 30
  sketch-geometry (4):
    g0: LineSegment StartX=-47.5 StartY=15 StartZ=0 EndX=47.5 EndY=15 EndZ=0
    g1: LineSegment StartX=47.5 StartY=15 StartZ=0 EndX=47.5 EndY=-15 EndZ=0
    g2: LineSegment StartX=47.5 StartY=-15 StartZ=0 EndX=-47.5 EndY=-15 EndZ=0
    g3: LineSegment StartX=-47.5 StartY=-15 StartZ=0 EndX=-47.5 EndY=15 EndZ=0
  constraints (10):
    c: Coincident(g0,g1)
    c: Coincident(g1,g2)
    c: Coincident(g2,g3)
    c: Coincident(g3,g0)
    c: Horizontal(g2)
    c: Vertical(g3)
    c: DistanceX(g0,g0) = 95
    c: Symmetric(g0,g0,g-2)
    c: Symmetric(g0,g1,g-1)
    c: DistanceY(g1,g1) = 30
FEATURE [PartDesign::Pad] Pad060
  Direction = (0,0,1)
  Length = 50
  Length2 = 10
  Profile = -> Sketch096
  ReferenceAxis = -> Sketch096 [N_Axis]
  Type = 0
FEATURE [Sketcher::SketchObject] Sketch097
  FullyConstrained = true
  MapMode = 5
  Support = -> [XY_Plane024]
  expr: Constraints[8] = Spreadsheet.breadboard_height + 2
  expr: Constraints[9] = Spreadsheet.breadboard_width + 2
  sketch-geometry (4):
    g0: LineSegment StartX=-28.5 StartY=6 StartZ=0 EndX=28.5 EndY=6 EndZ=0
    g1: LineSegment StartX=28.5 StartY=6 StartZ=0 EndX=28.5 EndY=-6 EndZ=0
    g2: LineSegment StartX=28.5 StartY=-6 StartZ=0 EndX=-28.5 EndY=-6 EndZ=0
    g3: LineSegment StartX=-28.5 StartY=-6 StartZ=0 EndX=-28.5 EndY=6 EndZ=0
  constraints (10):
    c: Coincident(g0,g1)
    c: Coincident(g1,g2)
    c: Coincident(g2,g3)
    c: Coincident(g3,g0)
    c: Horizontal(g2)
    c: Vertical(g1)
    c: Symmetric(g0,g0,g-2)
    c: Symmetric(g0,g2,g-1)
    c: DistanceX(g0,g0) = 57
    c: DistanceY(g3,g3) = 12
FEATURE [PartDesign::Pocket] Pocket030
  BaseFeature = -> Pad060
  Direction = (0,0,-1)
  Length = 5
  Length2 = 5
  Midplane = true
  Profile = -> Sketch097
  ReferenceAxis = -> Sketch097 [N_Axis]
  Type = 1
FEATURE [PartDesign::Plane] DatumPlane001
  AttachmentOffset = pos=(0,0,49) rot=(0,0,1;0rad)
  Length = 62.2474
  MapMode = 5
  Placement = pos=(49,-1.09e-14,1.09e-14) rot=(0.57735,0.57735,0.57735;2.0944rad)
  ResizeMode = 0
  Support = -> [YZ_Plane024]
  Width = 87.2474
FEATURE [Sketcher::SketchObject] Sketch098
  ExternalGeometry = -> [Pocket030]
  FullyConstrained = true
  MapMode = 5
  Placement = pos=(49,-1.09e-14,1.09e-14) rot=(0.57735,0.57735,0.57735;2.0944rad)
  Support = -> [DatumPlane001]
  sketch-geometry (4):
    g0: LineSegment StartX=-11 StartY=46 StartZ=0 EndX=11 EndY=46 EndZ=0
    g1: LineSegment StartX=11 StartY=46 StartZ=0 EndX=11 EndY=4 EndZ=0
    g2: LineSegment StartX=11 StartY=4 StartZ=0 EndX=-11 EndY=4 EndZ=0
    g3: LineSegment StartX=-11 StartY=4 StartZ=0 EndX=-11 EndY=46 EndZ=0
  constraints (12):
    c: Coincident(g0,g1)
    c: Coincident(g1,g2)
    c: Coincident(g2,g3)
    c: Coincident(g3,g0)
    c: Horizontal(g2)
    c: Vertical(g1)
    c: Vertical(g3)
    c: DistanceY(g1,g1) = 42
    c: Symmetric(g0,g0,g-2)
    c: DistanceX(g2,g1) = 22
    c: DistanceY(g-4,g-4) = 50
    c: DistanceY(g0,g-4) = 4
FEATURE [PartDesign::Pocket] Pocket031
  BaseFeature = -> Pocket030
  Direction = (-1,1e-16,-1e-16)
  Length = 5
  Length2 = 5
  Profile = -> Sketch098
  ReferenceAxis = -> Sketch098 [N_Axis]
  Type = 1
FEATURE [Sketcher::SketchObject] Sketch099
  FullyConstrained = false
  MapMode = 5
  Placement = pos=(49,-1.09e-14,1.09e-14) rot=(0.57735,0.57735,0.57735;2.0944rad)
  Support = -> [DatumPlane001]
  sketch-geometry (8):
    g0: LineSegment StartX=-3.26345 StartY=51.3519 StartZ=0 EndX=3.26345 EndY=51.3519 EndZ=0
    g1: LineSegment StartX=3.26345 StartY=51.3519 StartZ=0 EndX=3.26345 EndY=44.9769 EndZ=0
    g2: LineSegment StartX=3.26345 StartY=44.9769 StartZ=0 EndX=-3.26345 EndY=44.9769 EndZ=0
    g3: LineSegment StartX=-3.26345 StartY=44.9769 StartZ=0 EndX=-3.26345 EndY=51.3519 EndZ=0
    g4: LineSegment StartX=-3.26345 StartY=5.76119 StartZ=0 EndX=3.26345 EndY=5.76119 EndZ=0
    g5: LineSegment StartX=3.26345 StartY=5.76119 StartZ=0 EndX=3.26345 EndY=-3.31831 EndZ=0
    g6: LineSegment StartX=3.26345 StartY=-3.31831 StartZ=0 EndX=-3.26345 EndY=-3.31831 EndZ=0
    g7: LineSegment StartX=-3.26345 StartY=-3.31831 StartZ=0 EndX=-3.26345 EndY=5.76119 EndZ=0
  constraints (17):
    c: Coincident(g0,g1)
    c: Coincident(g1,g2)
    c: Coincident(g2,g3)
    c: Coincident(g3,g0)
    c: Horizontal(g2)
    c: Vertical(g1)
    c: Vertical(g3)
    c: Coincident(g4,g5)
    c: Coincident(g5,g6)
    c: Coincident(g6,g7)
    c: Coincident(g7,g4)
    c: Horizontal(g6)
    c: Vertical(g5)
    c: Vertical(g7)
    c: Symmetric(g4,g4,g-2)
    c: Symmetric(g0,g0,g-2)
    c: Equal(g0,g6)
FEATURE [PartDesign::Pocket] Pocket032
  BaseFeature = -> Pocket031
  Direction = (-1,1e-16,-1e-16)
  Length = 14
  Length2 = 5
  Profile = -> Sketch099
  ReferenceAxis = -> Sketch099 [N_Axis]
  Type = 0
FEATURE [PartDesign::Plane] DatumPlane002
  AttachmentOffset = pos=(0,0,-48) rot=(0,0,1;0rad)
  Length = 62.2474
  MapMode = 5
  Placement = pos=(-48,1.07e-14,-1.07e-14) rot=(0.57735,0.57735,0.57735;2.0944rad)
  ResizeMode = 0
  Support = -> [YZ_Plane024]
  Width = 87.2474
FEATURE [Sketcher::SketchObject] Sketch100
  FullyConstrained = false
  MapMode = 5
  Placement = pos=(-48,1.07e-14,-1.07e-14) rot=(0.57735,0.57735,0.57735;2.0944rad)
  Support = -> [DatumPlane002]
  sketch-geometry (8):
    g0: LineSegment StartX=-3.14361 StartY=50.7441 StartZ=0 EndX=3.14361 EndY=50.7441 EndZ=0
    g1: LineSegment StartX=3.14361 StartY=50.7441 StartZ=0 EndX=3.14361 EndY=40.7441 EndZ=0
    g2: LineSegment StartX=3.14361 StartY=40.7441 StartZ=0 EndX=-3.14361 EndY=40.7441 EndZ=0
    g3: LineSegment StartX=-3.14361 StartY=40.7441 StartZ=0 EndX=-3.14361 EndY=50.7441 EndZ=0
    g4: LineSegment StartX=-2.67337 StartY=4.52227 StartZ=0 EndX=3.61385 EndY=4.52227 EndZ=0
    g5: LineSegment StartX=3.61385 StartY=4.52227 StartZ=0 EndX=3.61385 EndY=-3.1146 EndZ=0
    g6: LineSegment StartX=3.61385 StartY=-3.1146 StartZ=0 EndX=-2.67337 EndY=-3.1146 EndZ=0
    g7: LineSegment StartX=-2.67337 StartY=-3.1146 StartZ=0 EndX=-2.67337 EndY=4.52227 EndZ=0
  constraints (18):
    c: Coincident(g0,g1)
    c: Coincident(g1,g2)
    c: Coincident(g2,g3)
    c: Coincident(g3,g0)
    c: Horizontal(g2)
    c: Vertical(g1)
    c: Vertical(g3)
    c: Coincident(g4,g5)
    c: Coincident(g5,g6)
    c: Coincident(g6,g7)
    c: Coincident(g7,g4)
    c: Horizontal(g4)
    c: Horizontal(g6)
    c: Vertical(g5)
    c: Vertical(g7)
    c: Equal(g0,g4)
    c: Symmetric(g0,g0,g-2)
    c: DistanceY(g1,g1) = 10
FEATURE [PartDesign::Pocket] Pocket033
  BaseFeature = -> Pocket032
  Direction = (-1,1e-16,-1e-16)
  Length = 13
  Length2 = 5
  Profile = -> Sketch100
  ReferenceAxis = -> Sketch100 [N_Axis]
  Reversed = true
  Type = 0
FEATURE [Sketcher::SketchObject] Sketch101
  ExternalGeometry = -> [Pocket033]
  FullyConstrained = false
  MapMode = 5
  Placement = pos=(0,15,0) rot=(0,0.707107,0.707107;3.14159rad)
  Support = -> [Pocket033]
  sketch-geometry (5):
    g0: Ellipse CenterX=0 CenterY=25 CenterZ=0 NormalX=0 NormalY=0 NormalZ=1 MajorRadius=29.6849 MinorRadius=17.9758 AngleXU=0
    g1: LineSegment StartX=29.6849 StartY=25 StartZ=0 EndX=-29.6849 EndY=25 EndZ=0
    g2: LineSegment StartX=-6e-16 StartY=42.9758 StartZ=0 EndX=6e-16 EndY=7.02421 EndZ=0
    g3: GeomPoint X=23.6234 Y=25 Z=0
    g4: GeomPoint X=-23.6234 Y=25 Z=0
  constraints (4):
    c: InternalAlignment(g1-g4 -> g0) x4
    c: PointOnObject(g0,g-2)
    c: Parallel(g1,g-1)
    c: DistanceY(g-1,g0) = 25
FEATURE [PartDesign::Pocket] Pocket034
  BaseFeature = -> Pocket033
  Direction = (0,-1,2e-16)
  Length = 5
  Length2 = 5
  Profile = -> Sketch101
  ReferenceAxis = -> Sketch101 [N_Axis]
  Type = 1
FEATURE [PartDesign::CoordinateSystem] Local_CS044
  AttacherType = Attacher::AttachEngine3D
  MapMode = 45
  Placement = pos=(-47.5,-0.0224957,25) rot=(0.57665,0.578747,0.57665;2.0923rad)
  Support = -> [Pocket034]
FEATURE [PartDesign::CoordinateSystem] Local_CS045
  AttacherType = Attacher::AttachEngine3D
  MapMode = 45
  Placement = pos=(-0.0616134,-0.0184245,0) rot=(0,0,1;1.57183rad)
  Support = -> [Pocket034]
FEATURE [PartDesign::CoordinateSystem] Local_CS046
  AttacherType = Attacher::AttachEngine3D
  MapMode = 45
  Placement = pos=(-0.0616134,-1.3e-15,50) rot=(0,0,1;1.5708rad)
  Support = -> [Pocket034]
FEATURE [PartDesign::CoordinateSystem] Local_CS047
  AttacherType = Attacher::AttachEngine3D
  MapMode = 45
  Placement = pos=(47.5,1.39e-14,25) rot=(0.57735,0.57735,0.57735;2.0944rad)
  Support = -> [Pocket034]
FEATURE [PartDesign::Body] Body022  label="leg_holder"
  Group = -> [Sketch096,Pad060,Sketch097,Pocket030,DatumPlane001,Sketch098,Pocket031,Sketch099,Pocket032,DatumPlane002,Sketch100,Pocket033,Sketch101,Pocket034,Local_CS044,Local_CS045,Local_CS046,Local_CS047]
  Origin = -> Origin024
  Tip = -> Pocket034
COMPONENT P10 — recipe-attached ("servo_lever_knee", modeled in this document).
Construction recipe (the document's own serialized feature program — sketch geometry with constraints, then the solid features built on it; lengths are millimeters unless a unit is written):

FEATURE [Sketcher::SketchObject] Sketch095
  FullyConstrained = true
  MapMode = 5
  Support = -> [XY_Plane027]
  sketch-geometry (6):
    g0: ArcOfCircle CenterX=0 CenterY=0 CenterZ=0 NormalX=0 NormalY=0 NormalZ=1 AngleXU=0 Radius=7.5 StartAngle=0.643501 EndAngle=5.63968
    g1: LineSegment StartX=6 StartY=4.5 StartZ=0 EndX=14 EndY=4.5 EndZ=0
    g2: LineSegment StartX=14 StartY=-4.5 StartZ=0 EndX=6 EndY=-4.5 EndZ=0
    g3: Circle CenterX=0 CenterY=0 CenterZ=0 NormalX=0 NormalY=0 NormalZ=1 AngleXU=0 Radius=3
    g4: ArcOfCircle CenterX=14 CenterY=0 CenterZ=0 NormalX=0 NormalY=0 NormalZ=1 AngleXU=0 Radius=4.5 StartAngle=4.71239 EndAngle=7.85398
    g5: Circle CenterX=11.5 CenterY=0 CenterZ=0 NormalX=0 NormalY=0 NormalZ=1 AngleXU=0 Radius=2
  constraints (17):
    c: Coincident(g0,g-1)
    c: Diameter(g0) = 15
    c: Horizontal(g1)
    c: Horizontal(g2)
    c: Coincident(g0,g2)
    c: Coincident(g0,g1)
    c: Coincident(g3,g0)
    c: Diameter(g3) = 6
    c: PointOnObject(g4,g-1)
    c: Tangent(g4,g1) = 1.5708
    c: Coincident(g4,g2)
    c: Diameter(g4) = 9
    c: PointOnObject(g5,g-1)
    c: Diameter(g5) = 4
    c: DistanceX(g0,g5) = 11.5
    c: DistanceX(g1,g1) = 8
    c: DistanceX(g2,g2) = 8
FEATURE [PartDesign::Pad] Pad059
  Direction = (0,0,1)
  Length = 4
  Length2 = 10
  Profile = -> Sketch095
  ReferenceAxis = -> Sketch095 [N_Axis]
  Type = 0
FEATURE [PartDesign::CoordinateSystem] Local_CS040
  AttacherType = Attacher::AttachEngine3D
  MapMode = 45
  Placement = pos=(-9e-16,0,2) rot=(0,0,1;0rad)
  Support = -> [Pad059]
FEATURE [PartDesign::CoordinateSystem] Local_CS041
  AttacherType = Attacher::AttachEngine3D
  MapMode = 45
  Placement = pos=(11.5,0,2) rot=(0,0,1;0rad)
  Support = -> [Pad059]
FEATURE [PartDesign::CoordinateSystem] Local_CS042
  AttacherType = Attacher::AttachEngine3D
  MapMode = 45
  Placement = pos=(4.42894,2e-15,0) rot=(0,0,1;1.5708rad)
  Support = -> [Pad059]
FEATURE [PartDesign::Body] Body023  label="servo_lever_knee"
  Group = -> [Sketch095,Pad059,Local_CS040,Local_CS041,Local_CS042]
  Origin = -> Origin027
  Tip = -> Pad059
COMPONENT P11 — recipe-attached ("leg_holder_breadboard_test", modeled in this document).
Construction recipe (the document's own serialized feature program — sketch geometry with constraints, then the solid features built on it; lengths are millimeters unless a unit is written):

FEATURE [Sketcher::SketchObject] Sketch102
  FullyConstrained = true
  MapMode = 5
  Support = -> [XY_Plane028]
  sketch-geometry (8):
    g0: LineSegment StartX=-27.5 StartY=5 StartZ=0 EndX=27.5 EndY=5 EndZ=0
    g1: LineSegment StartX=27.5 StartY=5 StartZ=0 EndX=27.5 EndY=-5 EndZ=0
    g2: LineSegment StartX=27.5 StartY=-5 StartZ=0 EndX=-27.5 EndY=-5 EndZ=0
    g3: LineSegment StartX=-27.5 StartY=-5 StartZ=0 EndX=-27.5 EndY=5 EndZ=0
    g4: LineSegment StartX=-40 StartY=8 StartZ=0 EndX=40 EndY=8 EndZ=0
    g5: LineSegment StartX=40 StartY=8 StartZ=0 EndX=40 EndY=-8 EndZ=0
    g6: LineSegment StartX=40 StartY=-8 StartZ=0 EndX=-40 EndY=-8 EndZ=0
    g7: LineSegment StartX=-40 StartY=-8 StartZ=0 EndX=-40 EndY=8 EndZ=0
  constraints (20):
    c: Coincident(g0,g1)
    c: Coincident(g1,g2)
    c: Coincident(g2,g3)
    c: Coincident(g3,g0)
    c: Horizontal(g2)
    c: Vertical(g3)
    c: Coincident(g4,g5)
    c: Coincident(g5,g6)
    c: Coincident(g6,g7)
    c: Coincident(g7,g4)
    c: Horizontal(g6)
    c: Vertical(g7)
    c: DistanceX(g0,g0) = 55
    c: DistanceY(g3,g3) = 10
    c: Symmetric(g0,g0,g-2)
    c: Symmetric(g0,g1,g-1)
    c: Symmetric(g4,g4,g-2)
    c: Symmetric(g4,g5,g-1)
    c: DistanceX(g4,g4) = 80
    c: DistanceY(g5,g5) = 16
FEATURE [PartDesign::Pad] Pad061
  Direction = (0,0,1)
  Length = 10
  Length2 = 10
  Profile = -> Sketch102
  ReferenceAxis = -> Sketch102 [N_Axis]
  Type = 0
FEATURE [Sketcher::SketchObject] Sketch103
  FullyConstrained = true
  MapMode = 5
  Placement = pos=(40,0,0) rot=(0.57735,0.57735,0.57735;2.0944rad)
  Support = -> [Pad061]
  sketch-geometry (4):
    g0: LineSegment StartX=-14.5 StartY=0 StartZ=0 EndX=14.5 EndY=0 EndZ=0
    g1: LineSegment StartX=14.5 StartY=0 StartZ=0 EndX=14.5 EndY=54 EndZ=0
    g2: LineSegment StartX=14.5 StartY=54 StartZ=0 EndX=-14.5 EndY=54 EndZ=0
    g3: LineSegment StartX=-14.5 StartY=54 StartZ=0 EndX=-14.5 EndY=0 EndZ=0
  constraints (11):
    c: Coincident(g0,g1)
    c: Coincident(g1,g2)
    c: Coincident(g2,g3)
    c: Coincident(g3,g0)
    c: Horizontal(g0)
    c: Vertical(g1)
    c: Vertical(g3)
    c: PointOnObject(g0,g-1)
    c: Symmetric(g1,g2,g-2)
    c: DistanceY(g1,g1) = 54
    c: DistanceX(g2,g2) = 29
FEATURE [PartDesign::Pad] Pad062
  BaseFeature = -> Pad061
  Direction = (1,0,0)
  Length = 4
  Length2 = 10
  Profile = -> Sketch103
  ReferenceAxis = -> Sketch103 [N_Axis]
  Type = 0
FEATURE [Sketcher::SketchObject] Sketch104
  ExternalGeometry = -> [Pad062]
  FullyConstrained = true
  MapMode = 5
  Placement = pos=(44,0,0) rot=(0.57735,0.57735,0.57735;2.0944rad)
  Support = -> [Pad062]
  sketch-geometry (8):
    g0: LineSegment StartX=-14.5 StartY=54 StartZ=0 EndX=-10.5 EndY=54 EndZ=0
    g1: LineSegment StartX=-10.5 StartY=54 StartZ=0 EndX=-10.5 EndY=0 EndZ=0
    g2: LineSegment StartX=-10.5 StartY=0 StartZ=0 EndX=-14.5 EndY=0 EndZ=0
    g3: LineSegment StartX=-14.5 StartY=0 StartZ=0 EndX=-14.5 EndY=54 EndZ=0
    g4: LineSegment StartX=14.5 StartY=0 StartZ=0 EndX=10.5 EndY=0 EndZ=0
    g5: LineSegment StartX=10.5 StartY=0 StartZ=0 EndX=10.5 EndY=54 EndZ=0
    g6: LineSegment StartX=10.5 StartY=54 StartZ=0 EndX=14.5 EndY=54 EndZ=0
    g7: LineSegment StartX=14.5 StartY=54 StartZ=0 EndX=14.5 EndY=0 EndZ=0
  constraints (22):
    c: Coincident(g0,g1)
    c: Coincident(g1,g2)
    c: Coincident(g2,g3)
    c: Coincident(g3,g0)
    c: Horizontal(g0)
    c: Horizontal(g2)
    c: Vertical(g1)
    c: Vertical(g3)
    c: Coincident(g0,g-4)
    c: PointOnObject(g1,g-1)
    c: Coincident(g4,g5)
    c: Coincident(g5,g6)
    c: Coincident(g6,g7)
    c: Coincident(g7,g4)
    c: Horizontal(g4)
    c: Horizontal(g6)
    c: Vertical(g5)
    c: Vertical(g7)
    c: Coincident(g4,g-5)
    c: PointOnObject(g5,g-3)
    c: Equal(g6,g0)
    c: DistanceX(g0,g0) = 4
FEATURE [PartDesign::Pad] Pad063
  BaseFeature = -> Pad062
  Direction = (1,0,0)
  Length = 36
  Length2 = 10
  Profile = -> Sketch104
  ReferenceAxis = -> Sketch104 [N_Axis]
  Type = 0
FEATURE [Sketcher::SketchObject] Sketch105
  ExternalGeometry = -> [Pad063]
  FullyConstrained = true
  MapMode = 5
  Placement = pos=(0,14.5,0) rot=(0,0.707107,0.707107;3.14159rad)
  Support = -> [Pad063]
  sketch-geometry (2):
    g0: Circle CenterX=-76 CenterY=49 CenterZ=0 NormalX=0 NormalY=0 NormalZ=1 AngleXU=0 Radius=2
    g1: Circle CenterX=-76 CenterY=5 CenterZ=0 NormalX=0 NormalY=0 NormalZ=1 AngleXU=0 Radius=2
  constraints (6):
    c: DistanceX(g0,g-5) = 32
    c: DistanceX(g1,g-5) = 32
    c: Diameter(g0) = 4
    c: Diameter(g1) = 4
    c: DistanceY(g1,g0) = 44
    c: DistanceY(g-4,g1) = 5
FEATURE [PartDesign::Pocket] Pocket035
  BaseFeature = -> Pad063
  Direction = (0,-1,2e-16)
  Length = 5
  Length2 = 5
  Profile = -> Sketch105
  ReferenceAxis = -> Sketch105 [N_Axis]
  Type = 1
FEATURE [Sketcher::SketchObject] Sketch106
  ExternalGeometry = -> [Sketch103]
  FullyConstrained = false
  MapMode = 5
  Placement = pos=(-40,0,0) rot=(0.57735,-0.57735,-0.57735;2.0944rad)
  Support = -> [Pocket035]
  sketch-geometry (4):
    g0: LineSegment StartX=-14.5 StartY=54 StartZ=0 EndX=14.4657 EndY=54 EndZ=0
    g1: LineSegment StartX=14.4657 StartY=54 StartZ=0 EndX=14.4657 EndY=0 EndZ=0
    g2: LineSegment StartX=14.4657 StartY=0 StartZ=0 EndX=-14.5 EndY=0 EndZ=0
    g3: LineSegment StartX=-14.5 StartY=0 StartZ=0 EndX=-14.5 EndY=54 EndZ=0
  constraints (10):
    c: Coincident(g0,g1)
    c: Coincident(g1,g2)
    c: Coincident(g2,g3)
    c: Coincident(g3,g0)
    c: Horizontal(g0)
    c: Horizontal(g2)
    c: Vertical(g1)
    c: Vertical(g3)
    c: Coincident(g0,g-4)
    c: PointOnObject(g1,g-1)
FEATURE [PartDesign::Pad] Pad064
  BaseFeature = -> Pocket035
  Direction = (-1,0,0)
  Length = 4
  Length2 = 10
  Profile = -> Sketch106
  ReferenceAxis = -> Sketch106 [N_Axis]
  Type = 0
FEATURE [Sketcher::SketchObject] Sketch107
  ExternalGeometry = -> [Pad064]
  FullyConstrained = true
  MapMode = 5
  Placement = pos=(-44,0,0) rot=(0.57735,-0.57735,-0.57735;2.0944rad)
  Support = -> [Pad064]
  sketch-geometry (8):
    g0: LineSegment StartX=-14.5 StartY=54 StartZ=0 EndX=-10.5 EndY=54 EndZ=0
    g1: LineSegment StartX=-10.5 StartY=54 StartZ=0 EndX=-10.5 EndY=0 EndZ=0
    g2: LineSegment StartX=-10.5 StartY=0 StartZ=0 EndX=-14.5 EndY=0 EndZ=0
    g3: LineSegment StartX=-14.5 StartY=0 StartZ=0 EndX=-14.5 EndY=54 EndZ=0
    g4: LineSegment StartX=14.4657 StartY=0 StartZ=0 EndX=10.4657 EndY=0 EndZ=0
    g5: LineSegment StartX=10.4657 StartY=0 StartZ=0 EndX=10.4657 EndY=54 EndZ=0
    g6: LineSegment StartX=10.4657 StartY=54 StartZ=0 EndX=14.4657 EndY=54 EndZ=0
    g7: LineSegment StartX=14.4657 StartY=54 StartZ=0 EndX=14.4657 EndY=0 EndZ=0
  constraints (22):
    c: Coincident(g0,g1)
    c: Coincident(g1,g2)
    c: Coincident(g2,g3)
    c: Coincident(g3,g0)
    c: Horizontal(g0)
    c: Horizontal(g2)
    c: Vertical(g1)
    c: Vertical(g3)
    c: Coincident(g0,g-5)
    c: PointOnObject(g1,g-6)
    c: Coincident(g4,g5)
    c: Coincident(g5,g6)
    c: Coincident(g6,g7)
    c: Coincident(g7,g4)
    c: Horizontal(g4)
    c: Horizontal(g6)
    c: Vertical(g5)
    c: Vertical(g7)
    c: Coincident(g4,g-6)
    c: PointOnObject(g5,g-3)
    c: Equal(g6,g0)
    c: DistanceX(g6,g6) = 4
FEATURE [PartDesign::Pad] Pad065
  BaseFeature = -> Pad064
  Direction = (-1,0,0)
  Length = 36
  Length2 = 10
  Profile = -> Sketch107
  ReferenceAxis = -> Sketch107 [N_Axis]
  Type = 0
FEATURE [Sketcher::SketchObject] Sketch108
  ExternalGeometry = -> [Pad065]
  FullyConstrained = true
  MapMode = 5
  Placement = pos=(0,14.5,0) rot=(0,0.707107,0.707107;3.14159rad)
  Support = -> [Pad065]
  sketch-geometry (2):
    g0: Circle CenterX=76 CenterY=49 CenterZ=0 NormalX=0 NormalY=0 NormalZ=1 AngleXU=0 Radius=2
    g1: Circle CenterX=76 CenterY=5 CenterZ=0 NormalX=0 NormalY=0 NormalZ=1 AngleXU=0 Radius=2
  constraints (4):
    c: Diameter(g0) = 4
    c: Diameter(g1) = 4
    c: Symmetric(g0,g-3,g-2)
    c: Symmetric(g1,g-4,g-2)
FEATURE [PartDesign::Pocket] Pocket036
  BaseFeature = -> Pad065
  Direction = (0,-1,2e-16)
  Length = 5
  Length2 = 5
  Profile = -> Sketch108
  ReferenceAxis = -> Sketch108 [N_Axis]
  Type = 1
FEATURE [PartDesign::Chamfer] Chamfer
  Angle = 45
  Base = -> Pocket036 [Edge38,Edge14,Edge16,Edge47]
  BaseFeature = -> Pocket036
  ChamferType = 0
  FlipDirection = false
  Size = 6
  Size2 = 1
  SupportTransform = false
  UseAllEdges = false
FEATURE [PartDesign::Body] Body024  label="leg_holder_breadboard_test"
  Group = -> [Sketch102,Pad061,Sketch103,Pad062,Sketch104,Pad063,Sketch105,Pocket035,Sketch106,Pad064,Sketch107,Pad065,Sketch108,Pocket036,Chamfer]
  Origin = -> Origin028
  Tip = -> Chamfer
PROVENANCE & LICENSES
A FreeCAD (.FCStd) document from a public repository crawl; recipes are the document's own serialized feature recipes (and, for linked parts, companion documents' recipes).
License: as declared in the source repository (recorded in the dataset sidecar).
